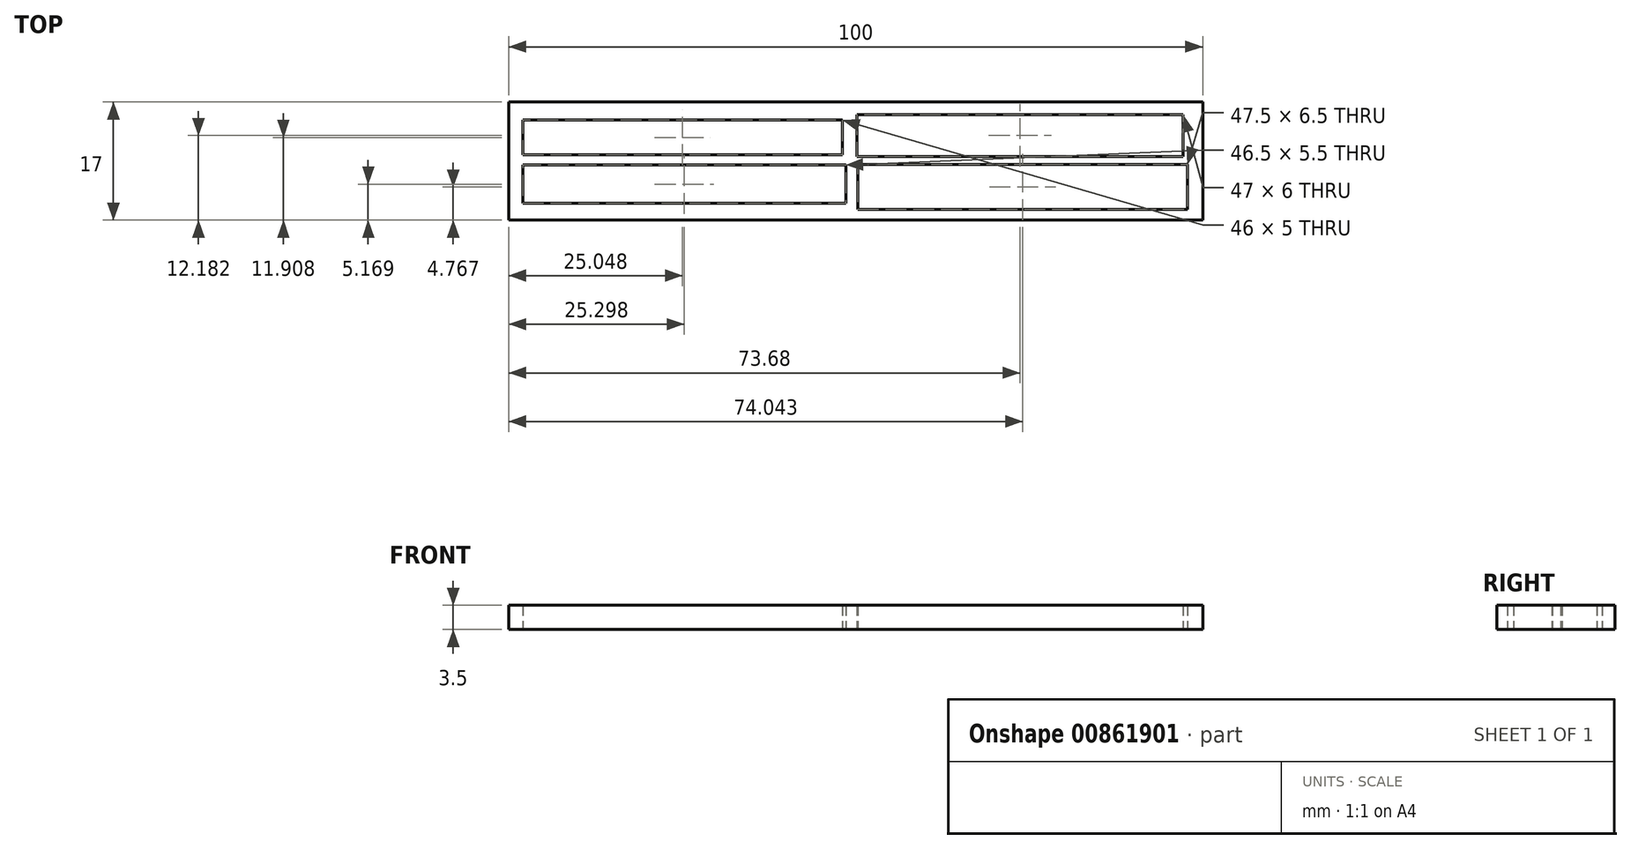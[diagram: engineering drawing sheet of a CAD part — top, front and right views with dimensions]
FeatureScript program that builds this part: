
annotation { "Feature Type Name" : "Feature", "Feature Type Description" : "" }
export const myFeature = defineFeature(function(context is Context, id is Id, definition is map)
    precondition{}
    {
        {
            var Q0;
            Q0=qCreatedBy(makeId("Top.planeOp"),FACE);
            var sketch = newSketch(context, id + "F0", { "sketchPlane" : qUnion([Q0])});
            skLineSegment(sketch, "E0.bottom", {"start": v(-51.48, 7.72) * mm, "end": v(48.52, 7.72) * mm});
            skLineSegment(sketch, "E0.top", {"start": v(-51.48, -9.28) * mm, "end": v(48.52, -9.28) * mm});
            skLineSegment(sketch, "E0.left", {"start": v(-51.48, 7.72) * mm, "end": v(-51.48, -9.28) * mm});
            skLineSegment(sketch, "E0.right", {"start": v(48.52, 7.72) * mm, "end": v(48.52, -9.28) * mm});
            skLineSegment(sketch, "E1.bottom", {"start": v(-49.43, 5.13) * mm, "end": v(-3.43, 5.13) * mm});
            skLineSegment(sketch, "E1.top", {"start": v(-49.43, 0.13) * mm, "end": v(-3.43, 0.13) * mm});
            skLineSegment(sketch, "E1.left", {"start": v(-49.43, 5.13) * mm, "end": v(-49.43, 0.13) * mm});
            skLineSegment(sketch, "E1.right", {"start": v(-3.43, 5.13) * mm, "end": v(-3.43, 0.13) * mm});
            skLineSegment(sketch, "E2.bottom", {"start": v(-1.3, 5.9) * mm, "end": v(45.7, 5.9) * mm});
            skLineSegment(sketch, "E2.top", {"start": v(-1.3, -0.1) * mm, "end": v(45.7, -0.1) * mm});
            skLineSegment(sketch, "E2.left", {"start": v(-1.3, 5.9) * mm, "end": v(-1.3, -0.1) * mm});
            skLineSegment(sketch, "E2.right", {"start": v(45.7, 5.9) * mm, "end": v(45.7, -0.1) * mm});
            skLineSegment(sketch, "E3.bottom", {"start": v(-49.43, -1.36) * mm, "end": v(-2.93, -1.36) * mm});
            skLineSegment(sketch, "E3.top", {"start": v(-49.43, -6.86) * mm, "end": v(-2.93, -6.86) * mm});
            skLineSegment(sketch, "E3.left", {"start": v(-49.43, -1.36) * mm, "end": v(-49.43, -6.86) * mm});
            skLineSegment(sketch, "E3.right", {"start": v(-2.93, -1.36) * mm, "end": v(-2.93, -6.86) * mm});
            skLineSegment(sketch, "E4.bottom", {"start": v(-1.19, -1.26) * mm, "end": v(46.31, -1.26) * mm});
            skLineSegment(sketch, "E4.top", {"start": v(-1.19, -7.76) * mm, "end": v(46.31, -7.76) * mm});
            skLineSegment(sketch, "E4.left", {"start": v(-1.19, -1.26) * mm, "end": v(-1.19, -7.76) * mm});
            skLineSegment(sketch, "E4.right", {"start": v(46.31, -1.26) * mm, "end": v(46.31, -7.76) * mm});
            skSolve(sketch);
        }
        {
            var Q0;
            Q0=makeQuery(id+"F0.imprint","IMPRINT",FACE,{"disambiguationData":[TD([[makeQuery(id+"F0.imprint","IMPRINT",EDGE,{"derivedFrom":sQuery(id+"F0.wireOp",EDGE,"E0.bottom")}),-1.0]])]});
            extrude(context, id + "F1", {"entities" : qUnion([Q0]), "depth" : 3.5 * mm, "offsetDistance" : 25 * mm});
        }
    });
